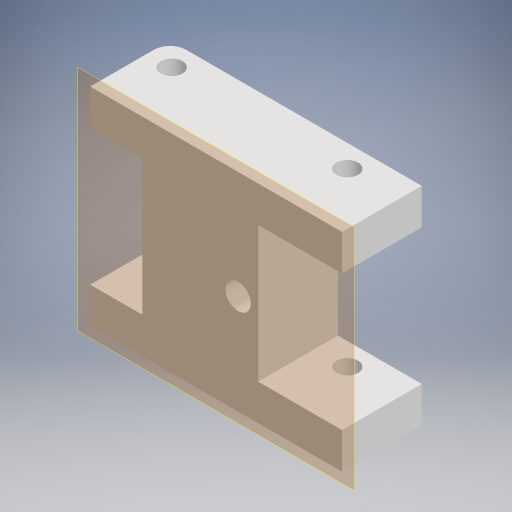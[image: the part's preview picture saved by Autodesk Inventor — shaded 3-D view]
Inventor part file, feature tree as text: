
AUTODESK INVENTOR PART (.ipt)
format: ipt  version: 2024 (Build 280153000, 153)  size: 253,440 bytes
history: native  units: in
note: dims shown in document units (in); Inventor stores cm internally (conversion verified against a paired STEP export)
features: other x4, extrude x2, sketch x2, reference x2, fillet x1
ambient origin geometry x8: Origin, YZ Plane, XZ Plane, XY Plane, X Axis, Y Axis, Z Axis, Center Point
bodies: Body1 (feature_tree)
feature tree (11):
  other  "솔리드1"
  other  "작업 평면2"
  extrude  "돌출1"  Depth=0.3937in TaperAngle=0.0deg
  extrude  "돌출2"  TaperAngle=0.0deg  [1 undecoded]
  fillet  "모깎기1"  Radius=0.0787in
  sketch  "스케치2"
  reference  "참조1"
  sketch  "스케치3"
  reference  "참조2"
  other  "조립품8"
  other  "foot_right_bottom_MIR_MIR_MIR:1"
note: 1 required parameter value undecoded (feature->parameter linkage not recoverable at this tier; creation-order binding heuristic only, values carry confidence <= 0.55)
